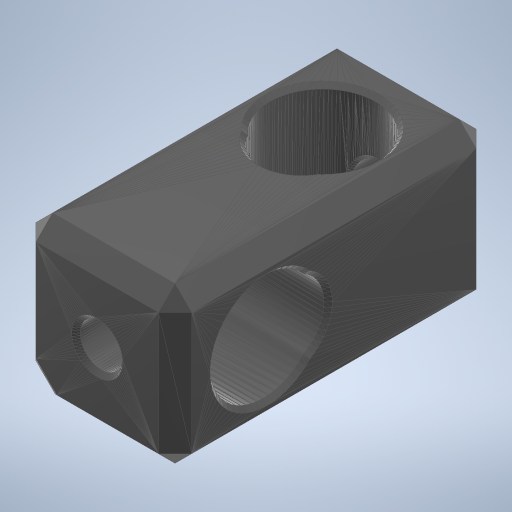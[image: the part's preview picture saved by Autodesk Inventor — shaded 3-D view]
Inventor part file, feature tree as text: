
AUTODESK INVENTOR PART (.ipt)
format: ipt  version: 2023 (Build 270158000, 158)  size: 309,248 bytes
history: native  units: in
note: dims shown in document units (in); Inventor stores cm internally (conversion verified against a paired STEP export)
features: other x2, sketch x2
ambient origin geometry x8: Origin, YZ Plane, XZ Plane, XY Plane, X Axis, Y Axis, Z Axis, Center Point
feature tree (4):
  other  "ra90k"
  sketch  "Sketch1"
  sketch  "Sketch2"
  other  "MeshFeature1"
